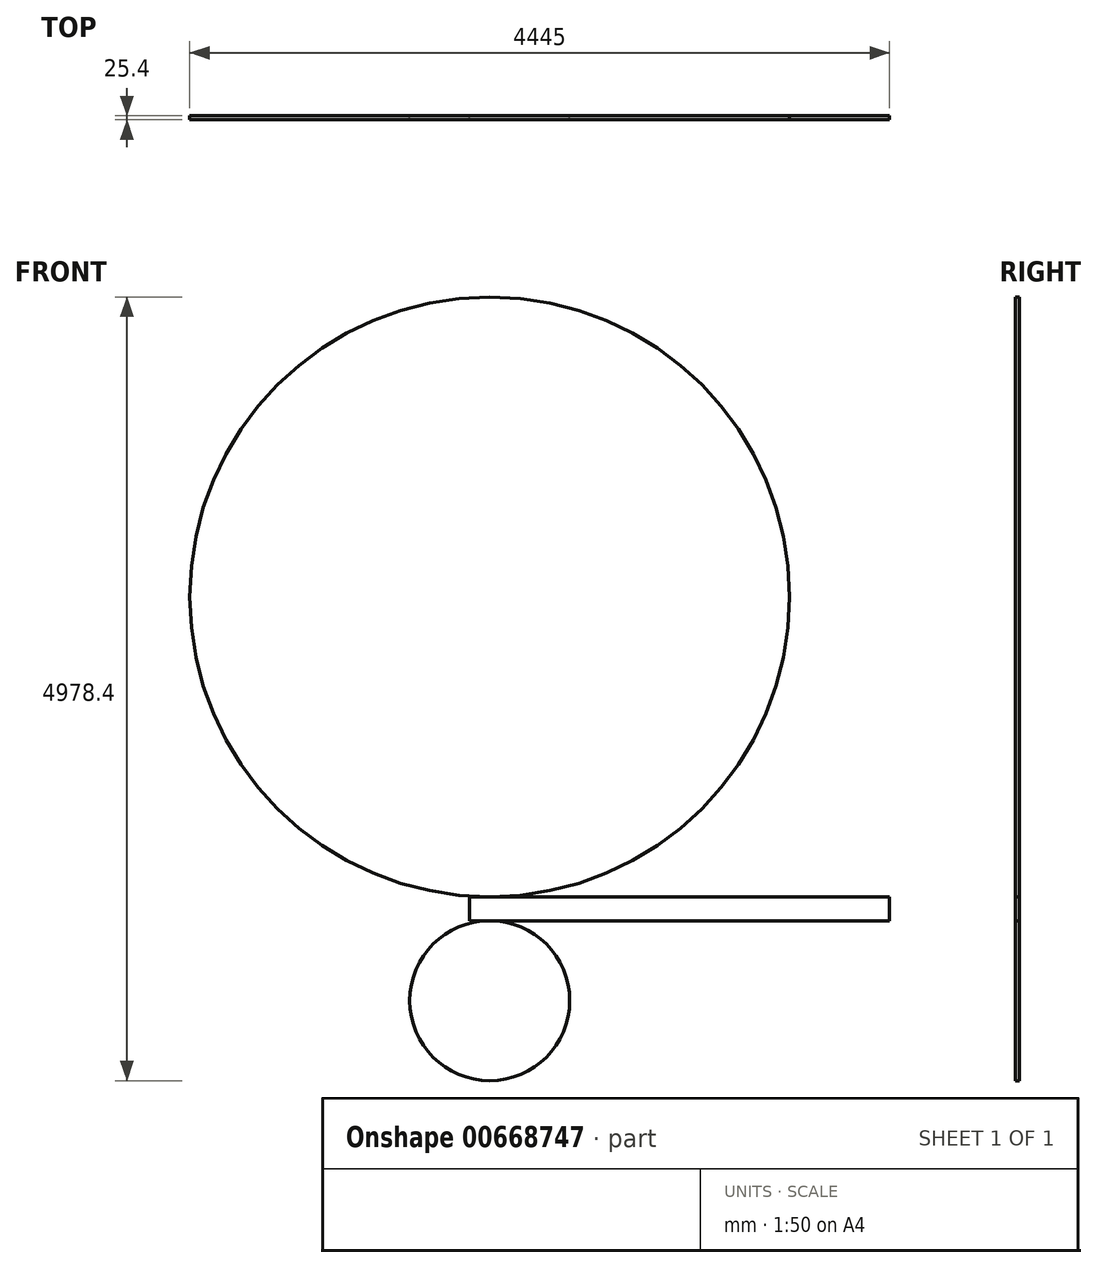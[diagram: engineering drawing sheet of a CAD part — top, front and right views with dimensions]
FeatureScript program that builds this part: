
annotation { "Feature Type Name" : "Feature", "Feature Type Description" : "" }
export const myFeature = defineFeature(function(context is Context, id is Id, definition is map)
    precondition{}
    {
        {
            var Q0;
            Q0=qCreatedBy(makeId("Front.planeOp"),FACE);
            var sketch = newSketch(context, id + "F0", { "sketchPlane" : qUnion([Q0])});
            skCircle(sketch, "E0", {"center": v(0, 1981.2) * mm, "radius": 1905 * mm});
            skCircle(sketch, "E1", {"center": v(0, -584.2) * mm, "radius": 508 * mm});
            skLineSegment(sketch, "E2.bottom", {"start": v(-127, 76.2) * mm, "end": v(2540, 76.2) * mm});
            skLineSegment(sketch, "E2.top", {"start": v(-127, -76.2) * mm, "end": v(2540, -76.2) * mm});
            skLineSegment(sketch, "E2.left", {"start": v(-127, 76.2) * mm, "end": v(-127, -76.2) * mm});
            skLineSegment(sketch, "E2.right", {"start": v(2540, 76.2) * mm, "end": v(2540, -76.2) * mm});
            skPoint(sketch, "E2.middle", {"position": v(1206.5, 0) * mm});
            skLineSegment(sketch, "E3", {"start": v(-127, 76.2) * mm, "end": v(-127, 80.44) * mm});
            skLineSegment(sketch, "E4", {"start": v(-127, -76.2) * mm, "end": v(-127, -92.33) * mm});
            skPoint(sketch, "E5", {"position": v(0, -76.2) * mm});
            skPoint(sketch, "E6", {"position": v(0, 76.2) * mm});
            skSolve(sketch);
        }
        {
            var Q0;
            Q0=makeQuery(id+"F0.imprint","IMPRINT",FACE,{"disambiguationData":[TD([[makeQuery(id+"F0.imprint","IMPRINT",EDGE,{"derivedFrom":sQuery(id+"F0.wireOp",EDGE,"E0")}),1.0]])]});
            var Q1;
            {var subQ3=sQuery(id+"F0.wireOp",EDGE,"E2.left");Q1=makeQuery(id+"F0.imprint","IMPRINT",FACE,{"disambiguationData":[TD([[makeQuery(id+"F0.imprint","IMPRINT",EDGE,{"derivedFrom":subQ3}),1.0]])]});}
            var Q2;
            Q2=makeQuery(id+"F0.imprint","IMPRINT",FACE,{"disambiguationData":[TD([[makeQuery(id+"F0.imprint","IMPRINT",EDGE,{"derivedFrom":sQuery(id+"F0.wireOp",EDGE,"E1")}),1.0]])]});
            extrude(context, id + "F1", {"entities" : qUnion([Q0, Q1, Q2]), "depth" : 25.4 * mm, "offsetDistance" : 25.4 * mm});
        }
    });
